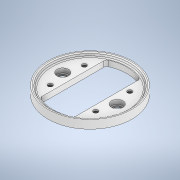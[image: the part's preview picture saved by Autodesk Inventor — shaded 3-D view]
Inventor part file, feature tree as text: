
AUTODESK INVENTOR PART (.ipt)
format: ipt  version: 2020 (Build 240168000, 168)  size: 188,416 bytes
history: native  units: in
note: dims shown in document units (in); Inventor stores cm internally (conversion verified against a paired STEP export)
features: sketch x4, fillet x2, hole x2, revolve x1, extrude x1
ambient origin geometry x8: Origin, YZ Plane, XZ Plane, XY Plane, X Axis, Y Axis, Z Axis, Center Point
bodies: Solid1 (feature_tree)
feature tree (10):
  revolve  "Revolution1"  [1 undecoded]
  fillet  "Fillet1"  [1 undecoded]
  extrude  "Extrusion1"  TaperAngle=90.0deg  [1 undecoded]
  hole  "Hole1"  [1 undecoded]
  hole  "Hole2"  [1 undecoded]
  fillet  "Fillet2"  Radius=0.124in
  sketch  "Sketch1"  dims[d0=1.766in d2=0.375in d3=60.0deg]
  sketch  "Sketch2"  dims[d4=1.85in d5=90.0deg]
  sketch  "Sketch3"  dims[d6=0.0625in d7=0.125in]
  sketch  "Sketch4"  dims[d8=3.25in d9=1.5in d10=0.124in d11=0.0in d12=2.4in d13=0.35in d14=0.75in d15=0.51in d16=0.188in d17=0.5635in d18=1.0in d19=0.8108in d20=2.0in d21=1.5in d22=0.205in d23=0.75in d24=0.3438in d25=0.19in d26=0.5635in d27=1.0in d28=0.8108in d29=0.125in]
note: 5 required parameter values undecoded (feature->parameter linkage not recoverable at this tier; creation-order binding heuristic only, values carry confidence <= 0.55)